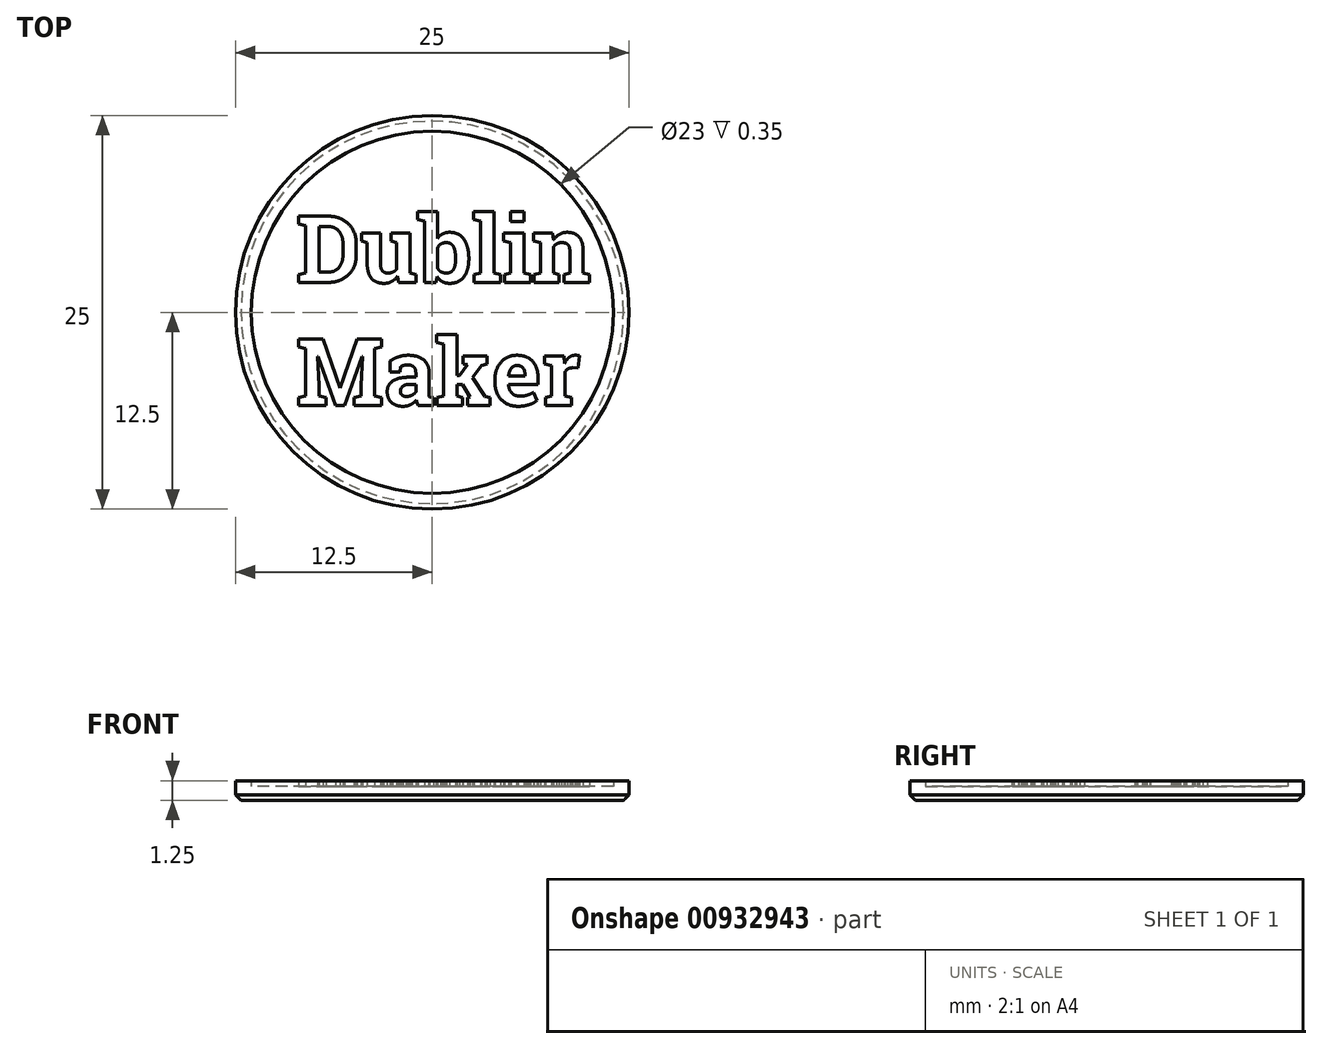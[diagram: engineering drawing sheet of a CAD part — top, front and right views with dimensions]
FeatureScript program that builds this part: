
annotation { "Feature Type Name" : "Feature", "Feature Type Description" : "" }
export const myFeature = defineFeature(function(context is Context, id is Id, definition is map)
    precondition{}
    {
        {
            var Q0;
            Q0=qCreatedBy(makeId("Top.planeOp"),FACE);
            var sketch = newSketch(context, id + "F0", { "sketchPlane" : qUnion([Q0])});
            skCircle(sketch, "E0", {"center": v(0, 0) * mm, "radius": 12.5 * mm});
            skCircle(sketch, "E1", {"center": v(0, 0) * mm, "radius": 11.5 * mm});
            skText(sketch, "E2", { "text": "Dublin\nMaker", "fontName": "RobotoSlab-Bold.ttf"});
            const initialGuessF0  = {"E2": [-0.00865, 0.0019, 1, 0, 0.00426]};
            skSetInitialGuess(sketch, initialGuessF0);
            skSolve(sketch);
        }
        {
            var Q0;
            Q0=makeQuery(id+"F0.imprint","IMPRINT",FACE,{"disambiguationData":[TD([[makeQuery(id+"F0.imprint","IMPRINT",EDGE,{"derivedFrom":sQuery(id+"F0.wireOp",EDGE,"E1")}),1.0]])]});
            var Q1;
            Q1=makeQuery(id+"F0.imprint","IMPRINT",FACE,{"disambiguationData":[TD([[makeQuery(id+"F0.imprint","IMPRINT",EDGE,{"derivedFrom":sQuery(id+"F0.wireOp",EDGE,"E0")}),1.0]])]});
            var Q2;
            Q2=makeQuery(id+"F0.imprint","IMPRINT",FACE,{"disambiguationData":[TD([[makeQuery(id+"F0.imprint","IMPRINT",EDGE,{"derivedFrom":sQuery(id+"F0.wireOp",EDGE,"E2.sketch_text.stroke-13")}),1.0]])]});
            var Q3;
            Q3=makeQuery(id+"F0.imprint","IMPRINT",FACE,{"disambiguationData":[TD([[makeQuery(id+"F0.imprint","IMPRINT",EDGE,{"derivedFrom":sQuery(id+"F0.wireOp",EDGE,"E2.sketch_text.stroke-231")}),1.0]])]});
            var Q4;
            Q4=makeQuery(id+"F0.imprint","IMPRINT",FACE,{"disambiguationData":[TD([[makeQuery(id+"F0.imprint","IMPRINT",EDGE,{"derivedFrom":sQuery(id+"F0.wireOp",EDGE,"E2.sketch_text.stroke-238")}),-1.0]])]});
            var Q5;
            Q5=makeQuery(id+"F0.imprint","IMPRINT",FACE,{"disambiguationData":[TD([[makeQuery(id+"F0.imprint","IMPRINT",EDGE,{"derivedFrom":sQuery(id+"F0.wireOp",EDGE,"E2.sketch_text.stroke-81")}),-1.0]])]});
            var Q6;
            Q6=makeQuery(id+"F0.imprint","IMPRINT",FACE,{"disambiguationData":[TD([[makeQuery(id+"F0.imprint","IMPRINT",EDGE,{"derivedFrom":sQuery(id+"F0.wireOp",EDGE,"E2.sketch_text.stroke-61")}),1.0]])]});
            var Q7;
            Q7=makeQuery(id+"F0.imprint","IMPRINT",FACE,{"disambiguationData":[TD([[makeQuery(id+"F0.imprint","IMPRINT",EDGE,{"derivedFrom":sQuery(id+"F0.wireOp",EDGE,"E2.sketch_text.stroke-187")}),-1.0]])]});
            var Q8;
            Q8=makeQuery(id+"F0.imprint","IMPRINT",FACE,{"disambiguationData":[TD([[makeQuery(id+"F0.imprint","IMPRINT",EDGE,{"derivedFrom":sQuery(id+"F0.wireOp",EDGE,"E2.sketch_text.stroke-21")}),-1.0]])]});
            var Q9;
            Q9=makeQuery(id+"F0.imprint","IMPRINT",FACE,{"disambiguationData":[TD([[makeQuery(id+"F0.imprint","IMPRINT",EDGE,{"derivedFrom":sQuery(id+"F0.wireOp",EDGE,"E2.sketch_text.stroke-214")}),-1.0]])]});
            var Q10;
            Q10=makeQuery(id+"F0.imprint","IMPRINT",FACE,{"disambiguationData":[TD([[makeQuery(id+"F0.imprint","IMPRINT",EDGE,{"derivedFrom":sQuery(id+"F0.wireOp",EDGE,"E2.sketch_text.stroke-179")}),1.0]])]});
            var Q11;
            Q11=makeQuery(id+"F0.imprint","IMPRINT",FACE,{"disambiguationData":[TD([[makeQuery(id+"F0.imprint","IMPRINT",EDGE,{"derivedFrom":sQuery(id+"F0.wireOp",EDGE,"E2.sketch_text.stroke-91")}),-1.0]])]});
            var Q12;
            Q12=makeQuery(id+"F0.imprint","IMPRINT",FACE,{"disambiguationData":[TD([[makeQuery(id+"F0.imprint","IMPRINT",EDGE,{"derivedFrom":sQuery(id+"F0.wireOp",EDGE,"E2.sketch_text.stroke-121")}),-1.0]])]});
            var Q13;
            Q13=makeQuery(id+"F0.imprint","IMPRINT",FACE,{"disambiguationData":[TD([[makeQuery(id+"F0.imprint","IMPRINT",EDGE,{"derivedFrom":sQuery(id+"F0.wireOp",EDGE,"E2.sketch_text.stroke-0")}),-1.0]])]});
            var Q14;
            Q14=makeQuery(id+"F0.imprint","IMPRINT",FACE,{"disambiguationData":[TD([[makeQuery(id+"F0.imprint","IMPRINT",EDGE,{"derivedFrom":sQuery(id+"F0.wireOp",EDGE,"E2.sketch_text.stroke-152")}),-1.0]])]});
            var Q15;
            Q15=makeQuery(id+"F0.imprint","IMPRINT",FACE,{"disambiguationData":[TD([[makeQuery(id+"F0.imprint","IMPRINT",EDGE,{"derivedFrom":sQuery(id+"F0.wireOp",EDGE,"E2.sketch_text.stroke-45")}),-1.0]])]});
            var Q16;
            Q16=makeQuery(id+"F0.imprint","IMPRINT",FACE,{"disambiguationData":[TD([[makeQuery(id+"F0.imprint","IMPRINT",EDGE,{"derivedFrom":sQuery(id+"F0.wireOp",EDGE,"E2.sketch_text.stroke-71")}),-1.0]])]});
            var Q17;
            Q17=makeQuery(id+"F0.imprint","IMPRINT",FACE,{"disambiguationData":[TD([[makeQuery(id+"F0.imprint","IMPRINT",EDGE,{"derivedFrom":sQuery(id+"F0.wireOp",EDGE,"E2.sketch_text.stroke-95")}),-1.0]])]});
            extrude(context, id + "F1", {"entities" : qUnion([Q0, Q1, Q2, Q3, Q4, Q5, Q6, Q7, Q8, Q9, Q10, Q11, Q12, Q13, Q14, Q15, Q16, Q17]), "depth" : (0.2 + 0.35 * 2) * mm, "offsetDistance" : 25 * mm});
        }
        {
            var Q0;
            Q0=makeQuery(id+"F0.imprint","IMPRINT",FACE,{"disambiguationData":[TD([[makeQuery(id+"F0.imprint","IMPRINT",EDGE,{"derivedFrom":sQuery(id+"F0.wireOp",EDGE,"E2.sketch_text.stroke-95")}),-1.0]])]});
            var Q1;
            Q1=makeQuery(id+"F0.imprint","IMPRINT",FACE,{"disambiguationData":[TD([[makeQuery(id+"F0.imprint","IMPRINT",EDGE,{"derivedFrom":sQuery(id+"F0.wireOp",EDGE,"E2.sketch_text.stroke-91")}),-1.0]])]});
            var Q2;
            Q2=makeQuery(id+"F0.imprint","IMPRINT",FACE,{"disambiguationData":[TD([[makeQuery(id+"F0.imprint","IMPRINT",EDGE,{"derivedFrom":sQuery(id+"F0.wireOp",EDGE,"E2.sketch_text.stroke-81")}),-1.0]])]});
            var Q3;
            Q3=makeQuery(id+"F0.imprint","IMPRINT",FACE,{"disambiguationData":[TD([[makeQuery(id+"F0.imprint","IMPRINT",EDGE,{"derivedFrom":sQuery(id+"F0.wireOp",EDGE,"E2.sketch_text.stroke-71")}),-1.0]])]});
            var Q4;
            Q4=makeQuery(id+"F0.imprint","IMPRINT",FACE,{"disambiguationData":[TD([[makeQuery(id+"F0.imprint","IMPRINT",EDGE,{"derivedFrom":sQuery(id+"F0.wireOp",EDGE,"E2.sketch_text.stroke-45")}),-1.0]])]});
            var Q5;
            Q5=makeQuery(id+"F0.imprint","IMPRINT",FACE,{"disambiguationData":[TD([[makeQuery(id+"F0.imprint","IMPRINT",EDGE,{"derivedFrom":sQuery(id+"F0.wireOp",EDGE,"E2.sketch_text.stroke-21")}),-1.0]])]});
            var Q6;
            Q6=makeQuery(id+"F0.imprint","IMPRINT",FACE,{"disambiguationData":[TD([[makeQuery(id+"F0.imprint","IMPRINT",EDGE,{"derivedFrom":sQuery(id+"F0.wireOp",EDGE,"E2.sketch_text.stroke-0")}),-1.0]])]});
            var Q7;
            Q7=makeQuery(id+"F0.imprint","IMPRINT",FACE,{"disambiguationData":[TD([[makeQuery(id+"F0.imprint","IMPRINT",EDGE,{"derivedFrom":sQuery(id+"F0.wireOp",EDGE,"E2.sketch_text.stroke-238")}),-1.0]])]});
            var Q8;
            Q8=makeQuery(id+"F0.imprint","IMPRINT",FACE,{"disambiguationData":[TD([[makeQuery(id+"F0.imprint","IMPRINT",EDGE,{"derivedFrom":sQuery(id+"F0.wireOp",EDGE,"E2.sketch_text.stroke-214")}),-1.0]])]});
            var Q9;
            Q9=makeQuery(id+"F0.imprint","IMPRINT",FACE,{"disambiguationData":[TD([[makeQuery(id+"F0.imprint","IMPRINT",EDGE,{"derivedFrom":sQuery(id+"F0.wireOp",EDGE,"E2.sketch_text.stroke-187")}),-1.0]])]});
            var Q10;
            Q10=makeQuery(id+"F0.imprint","IMPRINT",FACE,{"disambiguationData":[TD([[makeQuery(id+"F0.imprint","IMPRINT",EDGE,{"derivedFrom":sQuery(id+"F0.wireOp",EDGE,"E2.sketch_text.stroke-152")}),-1.0]])]});
            var Q11;
            Q11=makeQuery(id+"F0.imprint","IMPRINT",FACE,{"disambiguationData":[TD([[makeQuery(id+"F0.imprint","IMPRINT",EDGE,{"derivedFrom":sQuery(id+"F0.wireOp",EDGE,"E2.sketch_text.stroke-121")}),-1.0]])]});
            var Q12;
            Q12=makeQuery(id+"F0.imprint","IMPRINT",FACE,{"disambiguationData":[TD([[makeQuery(id+"F0.imprint","IMPRINT",EDGE,{"derivedFrom":sQuery(id+"F0.wireOp",EDGE,"E0")}),1.0]])]});
            extrude(context, id + "F2", {"entities" : qUnion([Q0, Q1, Q2, Q3, Q4, Q5, Q6, Q7, Q8, Q9, Q10, Q11, Q12]), "operationType" : NewBodyOperationType.ADD, "depth" : (0.2 + 0.35 * 3) * mm, "offsetDistance" : 25 * mm});
        }
        {
            var Q0;
            Q0=makeQuery(id+"F1.opExtrude","CAP_FACE",FACE,{"disambiguationData":[OSD([sQuery(id+"F0.wireOp",EDGE,"E0")])],"isStart":true});
            chamfer(context, id + "F3", {"entities" : qUnion([Q0]), "width" : 0.35 * mm, "tangentPropagation" : true});
        }
    });
